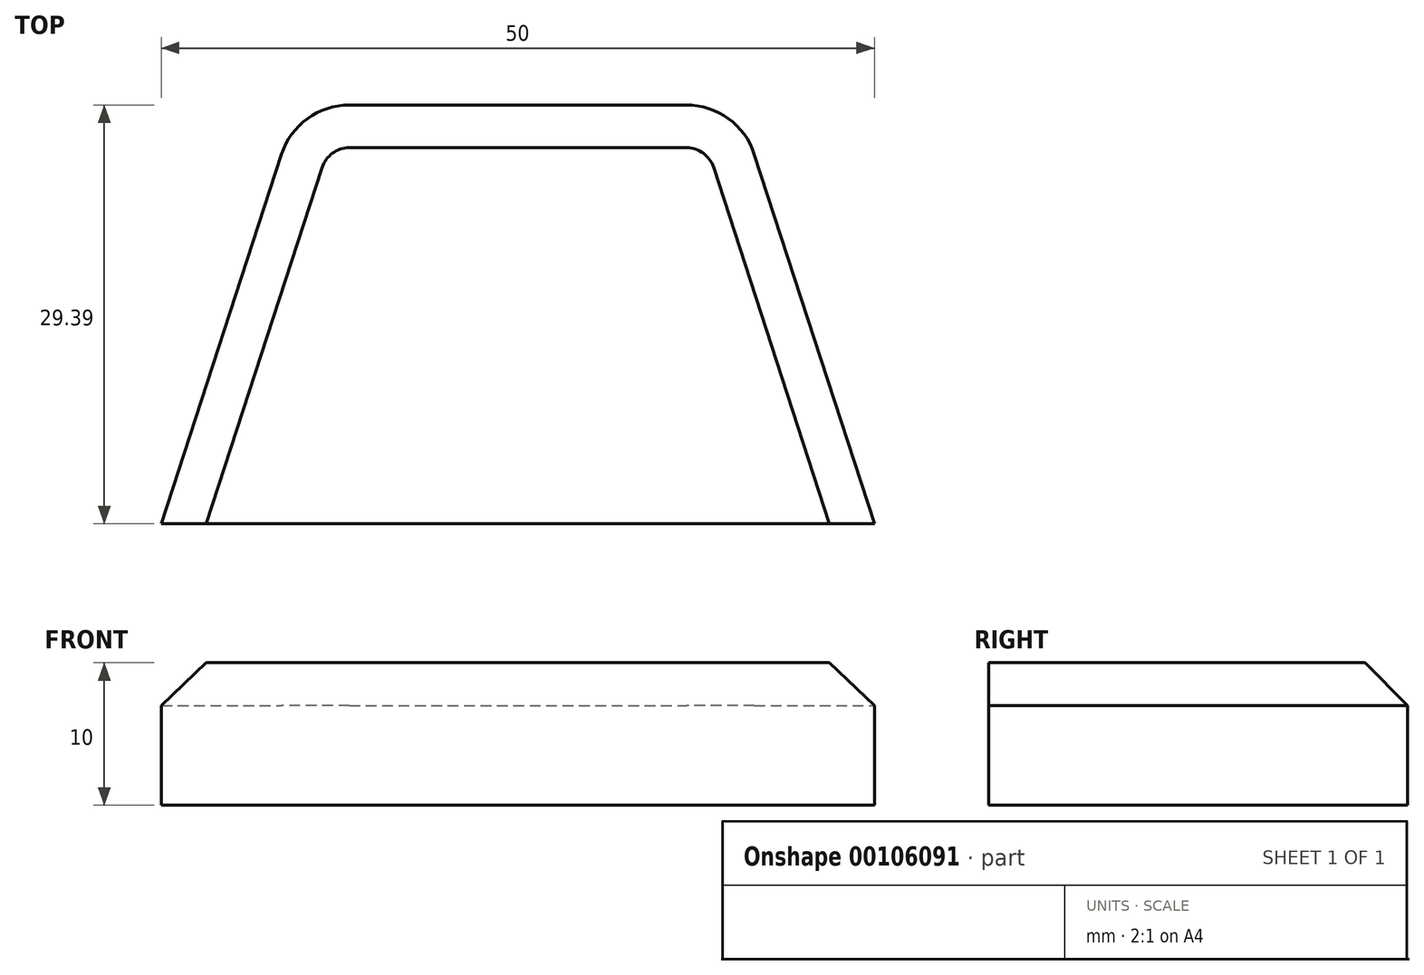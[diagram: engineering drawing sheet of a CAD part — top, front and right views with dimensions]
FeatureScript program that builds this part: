
annotation { "Feature Type Name" : "Feature", "Feature Type Description" : "" }
export const myFeature = defineFeature(function(context is Context, id is Id, definition is map)
    precondition{}
    {
        {
            var Q0;
            Q0=qCreatedBy(makeId("Top.planeOp"),FACE);
            var sketch = newSketch(context, id + "F0", { "sketchPlane" : qUnion([Q0])});
            skArc(sketch, "E0.cCircle", {"start": v(19.65, -8.12) * mm, "mid": v(0, 21.27) * mm, "end": v(-19.65, -8.12) * mm, "construction": true});
            skLineSegment(sketch, "E0.0", {"start": v(15.45, 21.27) * mm, "end": v(25, -8.12) * mm});
            skLineSegment(sketch, "E0.3", {"start": v(-25, -8.12) * mm, "end": v(-15.45, 21.27) * mm});
            skLineSegment(sketch, "E0.4", {"start": v(-15.45, 21.27) * mm, "end": v(15.45, 21.27) * mm});
            skPoint(sketch, "E0.0.midPoint", {"position": v(20.23, 6.57) * mm});
            skLineSegment(sketch, "E1", {"start": v(-25, -8.12) * mm, "end": v(25, -8.12) * mm});
            skSolve(sketch);
        }
        {
            var Q0;
            Q0=makeQuery(id+"F0.imprint","IMPRINT",FACE,{"disambiguationData":[TD([[makeQuery(id+"F0.imprint","IMPRINT",EDGE,{"derivedFrom":sQuery(id+"F0.wireOp",EDGE,"E0.0")}),-1.0]])]});
            extrude(context, id + "F1", {"entities" : qUnion([Q0]), "depth" : 10 * mm});
        }
        {
            var Q0;
            Q0=makeQuery(id+"F1.opExtrude","SWEPT_EDGE",EDGE,{"disambiguationData":[OSD([sQuery(id+"F0.wireOp",EDGE,"E0.0"),sQuery(id+"F0.wireOp",EDGE,"E0.4")])]});
            var Q1;
            Q1=makeQuery(id+"F1.opExtrude","SWEPT_EDGE",EDGE,{"disambiguationData":[OSD([sQuery(id+"F0.wireOp",EDGE,"E0.3"),sQuery(id+"F0.wireOp",EDGE,"E0.4")])]});
            fillet(context, id + "F2", {"entities" : qUnion([Q0, Q1]), "radius" : 5 * mm, "tangentPropagation" : true, "allowEdgeOverflow" : false});
        }
        {
            var Q0;
            Q0=makeQuery(id+"F1.opExtrude","CAP_EDGE",EDGE,{"disambiguationData":[OSD([sQuery(id+"F0.wireOp",EDGE,"E0.3")])],"isStart":false});
            var Q1;
            {var subQ0=sQuery(id+"F0.wireOp",EDGE,"E0.4");var subQ1=sQuery(id+"F0.wireOp",EDGE,"E0.3");Q1=makeQuery(id+"F2.opFillet","BLEND_EDGE",EDGE,{"blendedFrom":[makeQuery(id+"F1.opExtrude","SWEPT_EDGE",EDGE,{"disambiguationData":[OSD([subQ1,subQ0])]}),makeQuery(id+"F1.opExtrude","CAP_FACE",FACE,{"disambiguationData":[OSD([sQuery(id+"F0.wireOp",EDGE,"E0.0"),subQ1,subQ0,sQuery(id+"F0.wireOp",EDGE,"E1")])],"isStart":false})],"blendedInto":[makeQuery(id+"F1.opExtrude","CAP_FACE",FACE,{"disambiguationData":[OSD([sQuery(id+"F0.wireOp",EDGE,"E0.0"),subQ1,subQ0,sQuery(id+"F0.wireOp",EDGE,"E1")])],"isStart":false})]});}
            var Q2;
            Q2=makeQuery(id+"F1.opExtrude","CAP_EDGE",EDGE,{"disambiguationData":[OSD([sQuery(id+"F0.wireOp",EDGE,"E0.4")])],"isStart":false});
            var Q3;
            {var subQ0=sQuery(id+"F0.wireOp",EDGE,"E0.4");var subQ1=sQuery(id+"F0.wireOp",EDGE,"E0.0");Q3=makeQuery(id+"F2.opFillet","BLEND_EDGE",EDGE,{"blendedFrom":[makeQuery(id+"F1.opExtrude","SWEPT_EDGE",EDGE,{"disambiguationData":[OSD([subQ1,subQ0])]}),makeQuery(id+"F1.opExtrude","CAP_FACE",FACE,{"disambiguationData":[OSD([subQ1,sQuery(id+"F0.wireOp",EDGE,"E0.3"),subQ0,sQuery(id+"F0.wireOp",EDGE,"E1")])],"isStart":false})],"blendedInto":[makeQuery(id+"F1.opExtrude","CAP_FACE",FACE,{"disambiguationData":[OSD([subQ1,sQuery(id+"F0.wireOp",EDGE,"E0.3"),subQ0,sQuery(id+"F0.wireOp",EDGE,"E1")])],"isStart":false})]});}
            var Q4;
            Q4=makeQuery(id+"F1.opExtrude","CAP_EDGE",EDGE,{"disambiguationData":[OSD([sQuery(id+"F0.wireOp",EDGE,"E0.0")])],"isStart":false});
            chamfer(context, id + "F3", {"entities" : qUnion([Q0, Q1, Q2, Q3, Q4]), "width" : 3 * mm, "tangentPropagation" : true});
        }
    });
